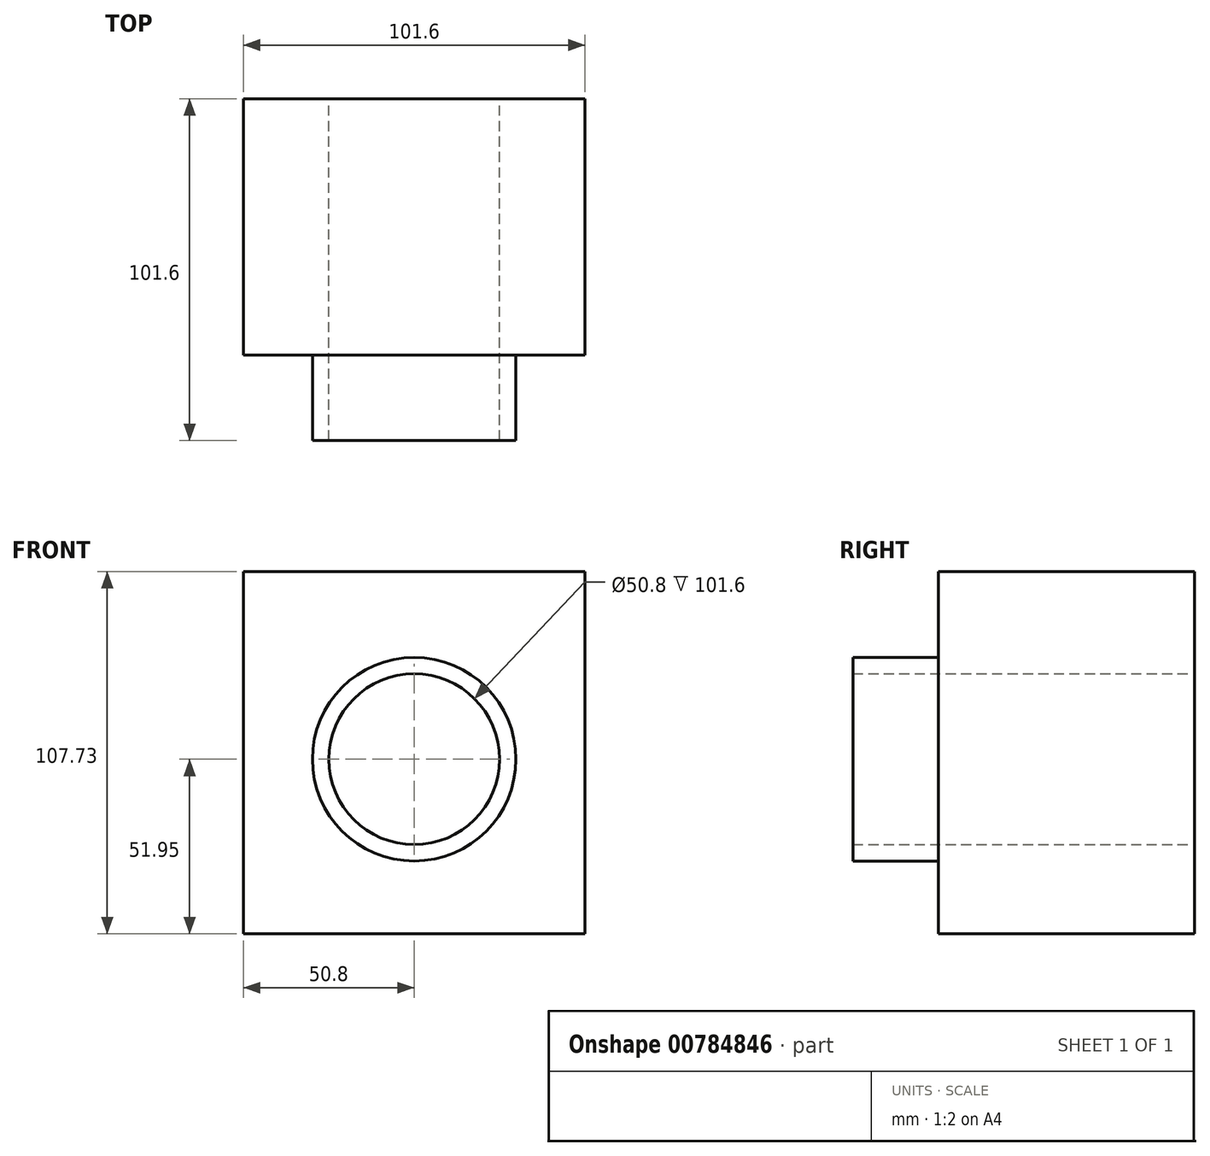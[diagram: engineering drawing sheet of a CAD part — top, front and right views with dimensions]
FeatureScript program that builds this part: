
annotation { "Feature Type Name" : "Feature", "Feature Type Description" : "" }
export const myFeature = defineFeature(function(context is Context, id is Id, definition is map)
    precondition{}
    {
        {
            var Q0;
            Q0=qCreatedBy(makeId("Front.planeOp"),FACE);
            var sketch = newSketch(context, id + "F0", { "sketchPlane" : qUnion([Q0])});
            skLineSegment(sketch, "E0.bottom", {"start": v(-50.8, 55.78) * mm, "end": v(50.8, 55.78) * mm});
            skLineSegment(sketch, "E0.top", {"start": v(-50.8, -51.95) * mm, "end": v(50.8, -51.95) * mm});
            skLineSegment(sketch, "E0.left", {"start": v(-50.8, 55.78) * mm, "end": v(-50.8, -51.95) * mm});
            skLineSegment(sketch, "E0.right", {"start": v(50.8, 55.78) * mm, "end": v(50.8, -51.95) * mm});
            skCircle(sketch, "E1", {"center": v(0, 0) * mm, "radius": 24.74 * mm});
            skCircle(sketch, "E2", {"center": v(0, 0) * mm, "radius": 19.9 * mm});
            skSolve(sketch);
        }
        {
            var Q0;
            Q0=qCreatedBy(makeId("Front.planeOp"),FACE);
            var sketch = newSketch(context, id + "F1", { "sketchPlane" : qUnion([Q0])});
            skCircle(sketch, "E3", {"center": v(0, 0) * mm, "radius": 30.27 * mm});
            skSolve(sketch);
        }
        {
            var Q0;
            Q0=makeQuery(id+"F0.imprint","IMPRINT",FACE,{"disambiguationData":[TD([[makeQuery(id+"F0.imprint","IMPRINT",EDGE,{"derivedFrom":sQuery(id+"F0.wireOp",EDGE,"E0.bottom")}),-1.0]])]});
            extrude(context, id + "F2", {"entities" : qUnion([Q0]), "depth" : 76.2 * mm, "offsetDistance" : 25.4 * mm});
        }
        {
            var Q0;
            Q0=makeQuery(id+"F1.imprint","IMPRINT",FACE,{"disambiguationData":[TD([[makeQuery(id+"F1.imprint","IMPRINT",EDGE,{"derivedFrom":sQuery(id+"F1.wireOp",EDGE,"E3")}),1.0]])]});
            extrude(context, id + "F3", {"entities" : qUnion([Q0]), "operationType" : NewBodyOperationType.ADD, "depth" : 101.6 * mm, "offsetDistance" : 25.4 * mm});
        }
        {
            var Q0;
            Q0=qCreatedBy(makeId("Front.planeOp"),FACE);
            var sketch = newSketch(context, id + "F4", { "sketchPlane" : qUnion([Q0])});
            skCircle(sketch, "E4", {"center": v(0, 0) * mm, "radius": 23.6 * mm});
            skSolve(sketch);
        }
        {
            var Q0;
            Q0=sQuery(id+"F4.wireOp",VERTEX,"E4.center");
            var Q1;
            Q1=makeQuery(id+"F2.opExtrude","SWEPT_BODY",BODY,{"disambiguationData":[OSD([sQuery(id+"F0.wireOp",EDGE,"E0.bottom"),sQuery(id+"F0.wireOp",EDGE,"E0.top"),sQuery(id+"F0.wireOp",EDGE,"E0.left"),sQuery(id+"F0.wireOp",EDGE,"E0.right"),sQuery(id+"F0.wireOp",EDGE,"E1")])]});
            hole(context, id + "F5", {"style" : HoleStyle.SIMPLE, "endStyle" : HoleEndStyle.THROUGH, "oppositeDirection" : true, "holeDiameter" : 50.8 * mm, "majorDiameter" : 6.35 * mm, "isTappedThrough" : true, "tappedDepth" : 12.7 * mm, "tapClearance" : 3, "locations" : qUnion([Q0]), "scope" : qUnion([Q1])});
        }
    });
